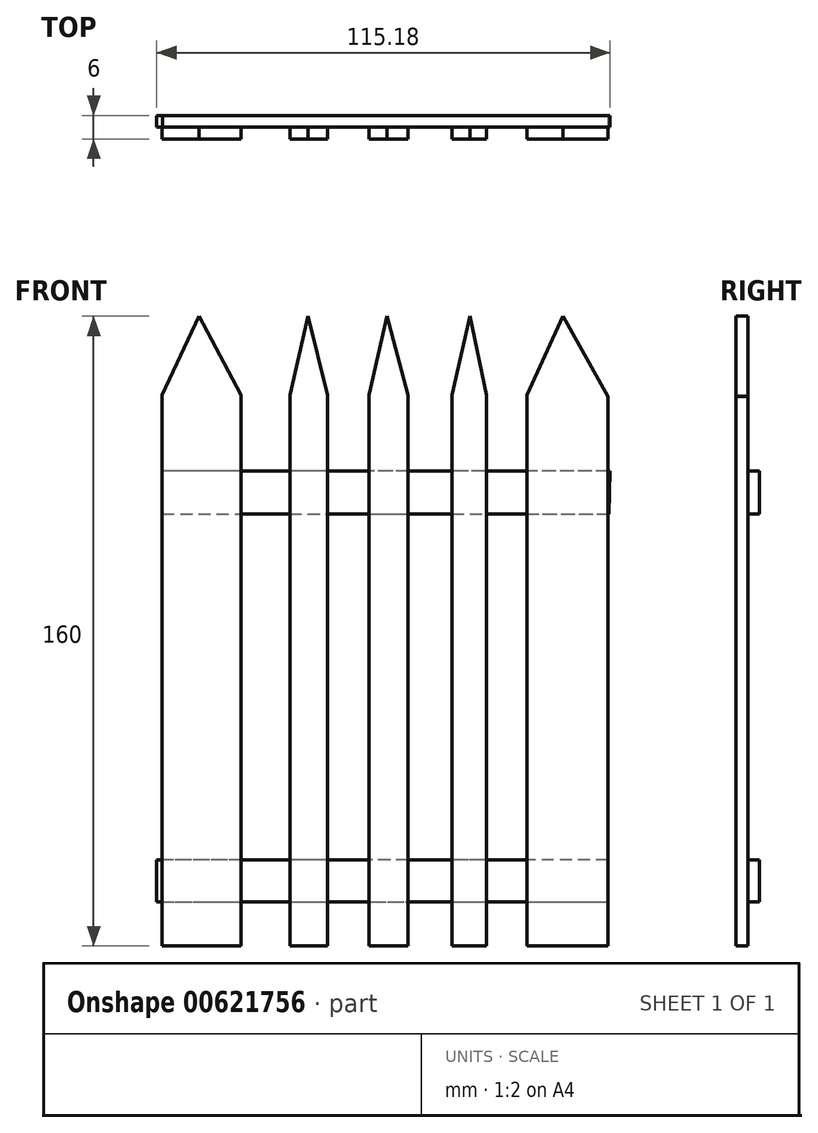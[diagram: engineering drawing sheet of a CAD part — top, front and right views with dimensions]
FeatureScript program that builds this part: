
annotation { "Feature Type Name" : "Feature", "Feature Type Description" : "" }
export const myFeature = defineFeature(function(context is Context, id is Id, definition is map)
    precondition{}
    {
        {
            var Q0;
            Q0=qCreatedBy(makeId("Front.planeOp"),FACE);
            var sketch = newSketch(context, id + "F0", { "sketchPlane" : qUnion([Q0])});
            skLineSegment(sketch, "E0", {"start": v(-78.42, -87.58) * mm, "end": v(-78.42, 52.42) * mm});
            skLineSegment(sketch, "E1", {"start": v(-78.42, -87.58) * mm, "end": v(-58.42, -87.58) * mm});
            skLineSegment(sketch, "E2", {"start": v(-58.42, -87.58) * mm, "end": v(-58.42, 52.42) * mm});
            skLineSegment(sketch, "E3", {"start": v(-46, -87.58) * mm, "end": v(-46, 52.42) * mm});
            skLineSegment(sketch, "E4", {"start": v(-46, -87.58) * mm, "end": v(-36.44, -87.58) * mm});
            skLineSegment(sketch, "E5", {"start": v(-36.44, -87.58) * mm, "end": v(-36.44, 52.42) * mm});
            skLineSegment(sketch, "E6", {"start": v(-25.85, -87.58) * mm, "end": v(-25.85, 52.42) * mm});
            skLineSegment(sketch, "E7", {"start": v(-25.85, -87.58) * mm, "end": v(-16.03, -87.58) * mm});
            skLineSegment(sketch, "E8", {"start": v(-16.03, -87.58) * mm, "end": v(-16.03, 52.42) * mm});
            skLineSegment(sketch, "E9", {"start": v(-4.83, -87.58) * mm, "end": v(-4.83, 52.42) * mm});
            skLineSegment(sketch, "E10", {"start": v(-4.83, -87.58) * mm, "end": v(3.92, -87.58) * mm});
            skLineSegment(sketch, "E11", {"start": v(3.92, -87.58) * mm, "end": v(3.92, 52.42) * mm});
            skLineSegment(sketch, "E12", {"start": v(14.21, -87.58) * mm, "end": v(14.21, 52.42) * mm});
            skLineSegment(sketch, "E13", {"start": v(-78.42, 52.42) * mm, "end": v(-69.04, 72.42) * mm});
            skLineSegment(sketch, "E14", {"start": v(-69.04, 72.42) * mm, "end": v(-58.42, 52.42) * mm});
            skLineSegment(sketch, "E15", {"start": v(-46, 52.42) * mm, "end": v(-41.43, 72.42) * mm});
            skLineSegment(sketch, "E16", {"start": v(-41.43, 72.42) * mm, "end": v(-36.44, 52.42) * mm});
            skLineSegment(sketch, "E17", {"start": v(-25.85, 52.42) * mm, "end": v(-21.28, 72.42) * mm});
            skLineSegment(sketch, "E18", {"start": v(-21.28, 72.42) * mm, "end": v(-16.03, 52.42) * mm});
            skLineSegment(sketch, "E19", {"start": v(-4.83, 52.42) * mm, "end": v(-0.27, 72.42) * mm});
            skLineSegment(sketch, "E20", {"start": v(-0.27, 72.42) * mm, "end": v(3.92, 52.42) * mm});
            skLineSegment(sketch, "E21", {"start": v(14.21, -87.58) * mm, "end": v(34.82, -87.58) * mm});
            skLineSegment(sketch, "E22", {"start": v(34.82, -87.58) * mm, "end": v(34.82, 51.96) * mm});
            skLineSegment(sketch, "E23", {"start": v(34.82, 51.96) * mm, "end": v(23.4, 72.42) * mm});
            skLineSegment(sketch, "E24", {"start": v(14.21, 52.42) * mm, "end": v(23.4, 72.42) * mm});
            skSolve(sketch);
        }
        {
            var Q0;
            Q0=makeQuery(id+"F0.imprint","IMPRINT",FACE,{"disambiguationData":[TD([[makeQuery(id+"F0.imprint","IMPRINT",EDGE,{"derivedFrom":sQuery(id+"F0.wireOp",EDGE,"E0")}),-1.0]])]});
            var sketch = newSketch(context, id + "F1", { "sketchPlane" : qUnion([Q0])});
            skSolve(sketch);
        }
        {
            var Q0;
            Q0=makeQuery(id+"F0.imprint","IMPRINT",FACE,{"disambiguationData":[TD([[makeQuery(id+"F0.imprint","IMPRINT",EDGE,{"derivedFrom":sQuery(id+"F0.wireOp",EDGE,"E3")}),-1.0]])]});
            var Q1;
            Q1=makeQuery(id+"F0.imprint","IMPRINT",FACE,{"disambiguationData":[TD([[makeQuery(id+"F0.imprint","IMPRINT",EDGE,{"derivedFrom":sQuery(id+"F0.wireOp",EDGE,"E0")}),-1.0]])]});
            var Q2;
            Q2=makeQuery(id+"F0.imprint","IMPRINT",FACE,{"disambiguationData":[TD([[makeQuery(id+"F0.imprint","IMPRINT",EDGE,{"derivedFrom":sQuery(id+"F0.wireOp",EDGE,"E9")}),-1.0]])]});
            var Q3;
            Q3=makeQuery(id+"F0.imprint","IMPRINT",FACE,{"disambiguationData":[TD([[makeQuery(id+"F0.imprint","IMPRINT",EDGE,{"derivedFrom":sQuery(id+"F0.wireOp",EDGE,"E6")}),-1.0]])]});
            var Q4;
            Q4=makeQuery(id+"F0.imprint","IMPRINT",FACE,{"disambiguationData":[TD([[makeQuery(id+"F0.imprint","IMPRINT",EDGE,{"derivedFrom":sQuery(id+"F0.wireOp",EDGE,"E12")}),-1.0]])]});
            var Q5;
            Q5=makeQuery(id+"F1.imprint","IMPRINT",FACE,{"disambiguationData":[TD([[makeQuery(id+"F1.imprint","IMPRINT",EDGE,{"derivedFrom":makeQuery(id+"F0.imprint","IMPRINT",EDGE,{"derivedFrom":sQuery(id+"F0.wireOp",EDGE,"E0")})}),-1.0]])]});
            extrude(context, id + "F2", {"entities" : qUnion([Q0, Q1, Q2, Q3, Q4, Q5]), "depth" : 3 * mm, "offsetDistance" : 25 * mm});
        }
        {
            var Q0;
            Q0=qCreatedBy(makeId("Front.planeOp"),FACE);
            var sketch = newSketch(context, id + "F3", { "sketchPlane" : qUnion([Q0])});
            skLineSegment(sketch, "E25", {"start": v(35.34, 33.06) * mm, "end": v(-78.38, 33.06) * mm});
            skLineSegment(sketch, "E26", {"start": v(-78.38, 33.06) * mm, "end": v(-78.38, 22.2) * mm});
            skLineSegment(sketch, "E27", {"start": v(-78.38, 22.2) * mm, "end": v(35.06, 22.2) * mm});
            skLineSegment(sketch, "E28", {"start": v(35.06, 22.2) * mm, "end": v(35.34, 33.06) * mm});
            skSolve(sketch);
        }
        {
            var Q0;
            Q0 = qSketchRegion(id + "F3", true);
            extrude(context, id + "F4", {"entities" : qUnion([Q0]), "depth" : -3 * mm, "offsetDistance" : 25 * mm});
        }
        {
            var Q0;
            Q0=makeQuery(id+"F2.opExtrude","CAP_FACE",FACE,{"disambiguationData":[OSD([sQuery(id+"F0.wireOp",EDGE,"E12"),sQuery(id+"F0.wireOp",EDGE,"E21"),sQuery(id+"F0.wireOp",EDGE,"E22"),sQuery(id+"F0.wireOp",EDGE,"E23"),sQuery(id+"F0.wireOp",EDGE,"E24")])],"isStart":true});
            var sketch = newSketch(context, id + "F5", { "sketchPlane" : qUnion([Q0])});
            skLineSegment(sketch, "E29", {"start": v(-34.82, -65.73) * mm, "end": v(79.84, -65.73) * mm});
            skLineSegment(sketch, "E30", {"start": v(79.84, -65.73) * mm, "end": v(79.84, -76.31) * mm});
            skLineSegment(sketch, "E31", {"start": v(79.84, -76.31) * mm, "end": v(-34.82, -76.31) * mm});
            skLineSegment(sketch, "E32", {"start": v(-34.82, -76.31) * mm, "end": v(-34.82, -65.73) * mm});
            skSolve(sketch);
        }
        {
            var Q0;
            Q0 = qSketchRegion(id + "F5", true);
            extrude(context, id + "F6", {"entities" : qUnion([Q0]), "depth" : 3 * mm, "offsetDistance" : 25 * mm});
        }
    });
